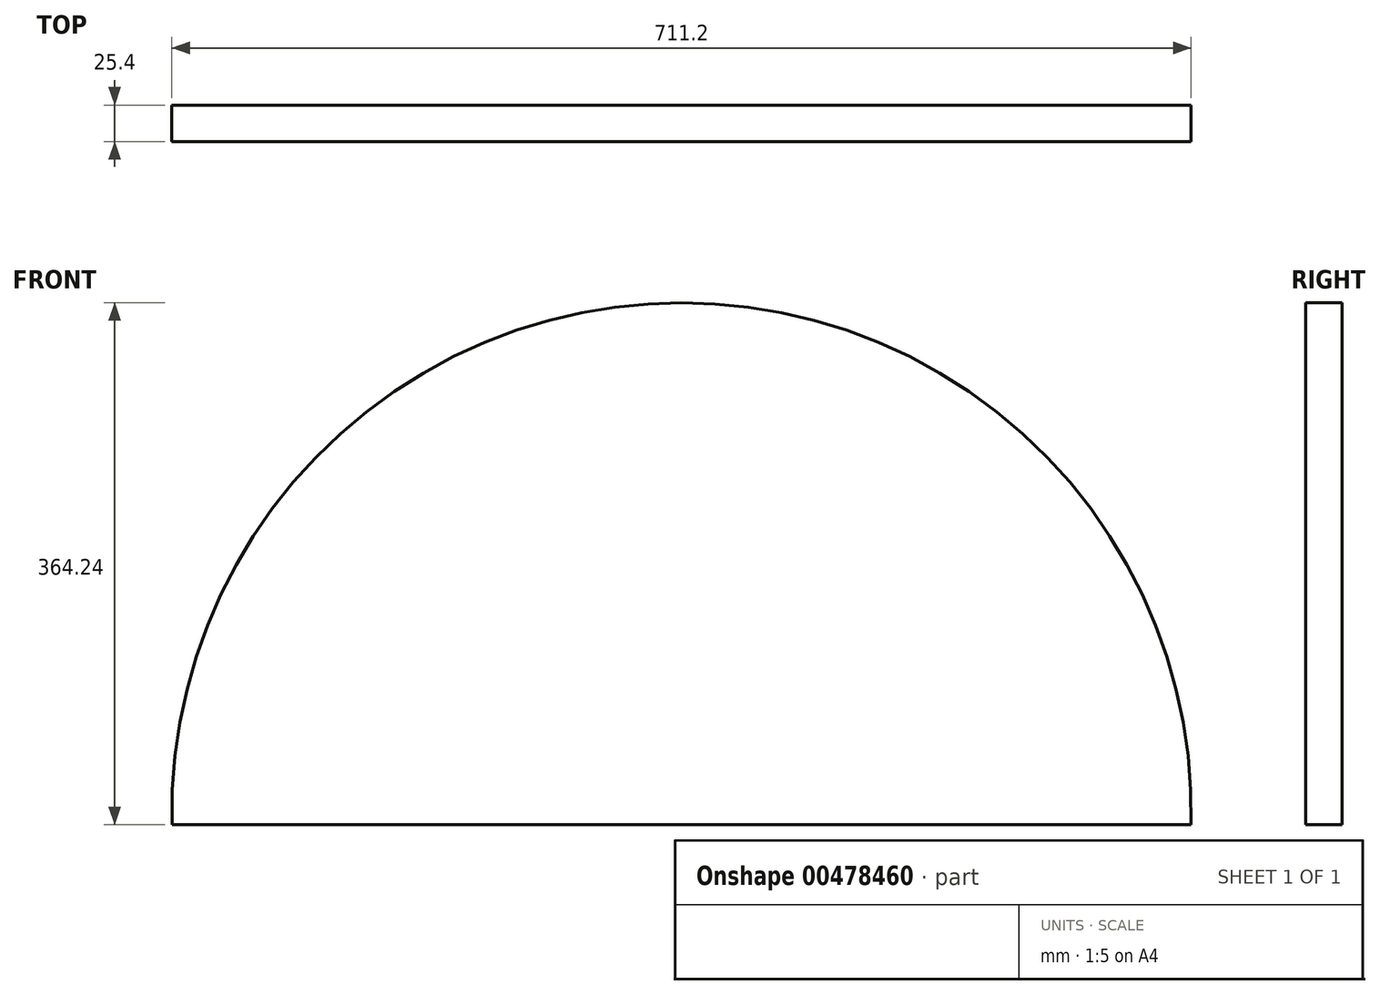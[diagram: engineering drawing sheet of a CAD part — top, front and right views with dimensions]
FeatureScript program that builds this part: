
annotation { "Feature Type Name" : "Feature", "Feature Type Description" : "" }
export const myFeature = defineFeature(function(context is Context, id is Id, definition is map)
    precondition{}
    {
        {
            var Q0;
            Q0=qCreatedBy(makeId("Front.planeOp"),FACE);
            var sketch = newSketch(context, id + "F0", { "sketchPlane" : qUnion([Q0])});
            skArc(sketch, "E0", {"start": v(711, 0) * mm, "mid": v(355.5, 364.24) * mm, "end": v(0, 0) * mm});
            skLineSegment(sketch, "E1", {"start": v(0, 0) * mm, "end": v(711, 0) * mm});
            skSolve(sketch);
        }
        {
            var Q0;
            Q0 = qSketchRegion(id + "F0", true);
            extrude(context, id + "F1", {"entities" : qUnion([Q0]), "depth" : 25.4 * mm});
        }
    });
